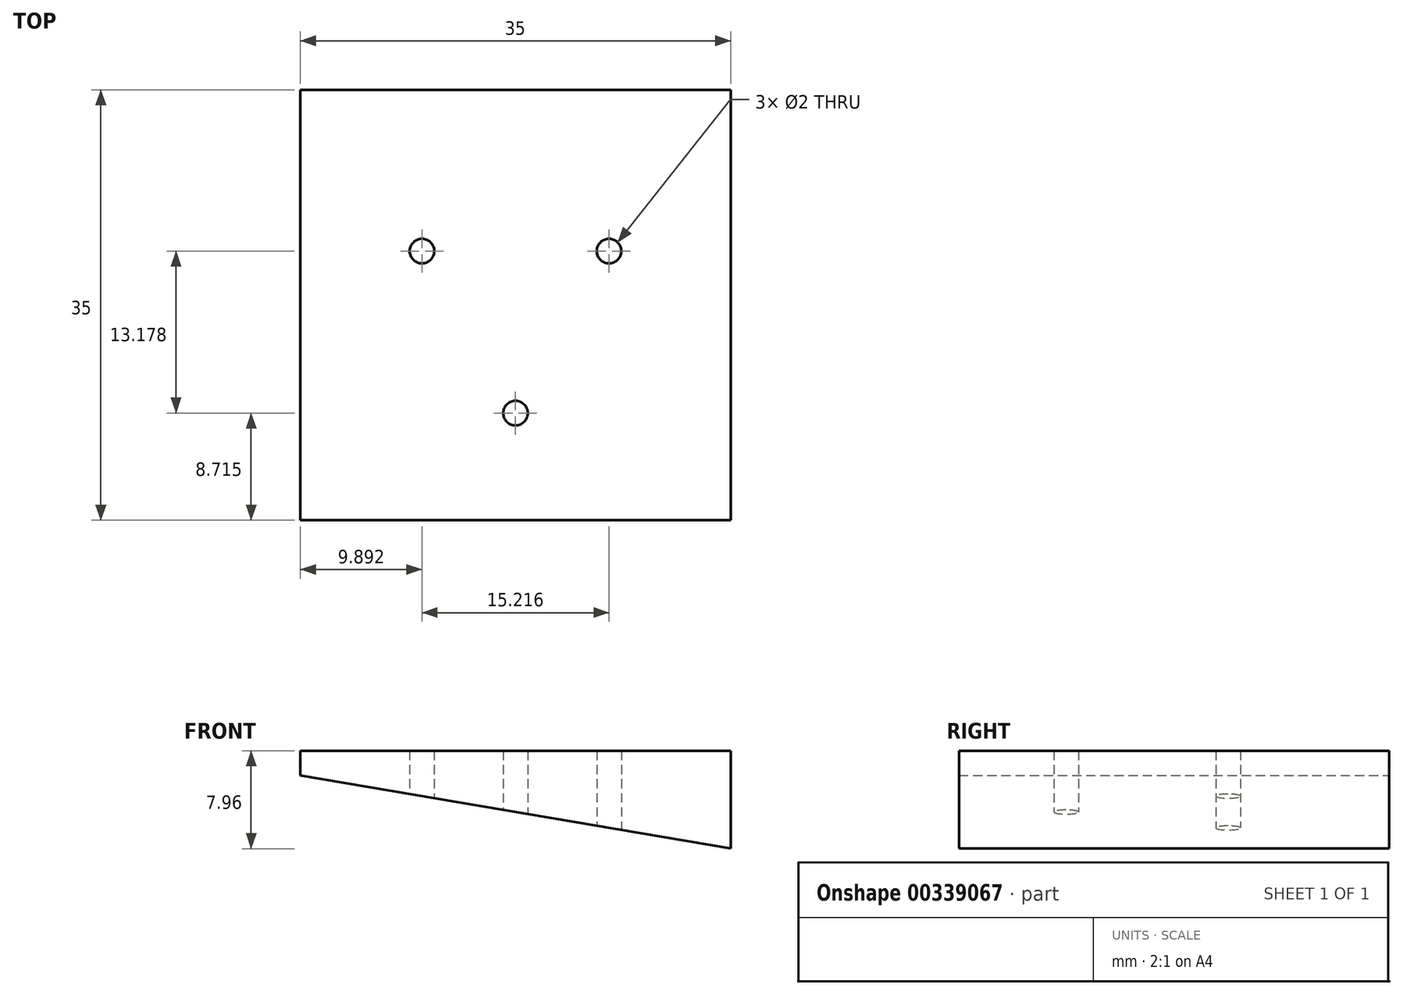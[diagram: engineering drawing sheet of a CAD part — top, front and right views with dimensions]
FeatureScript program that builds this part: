
annotation { "Feature Type Name" : "Feature", "Feature Type Description" : "" }
export const myFeature = defineFeature(function(context is Context, id is Id, definition is map)
    precondition{}
    {
        {
            var Q0;
            Q0=qCreatedBy(makeId("Top.planeOp"),FACE);
            var sketch = newSketch(context, id + "F0", { "sketchPlane" : qUnion([Q0])});
            skLineSegment(sketch, "E0.bottom", {"start": v(17.5, -17.5) * mm, "end": v(-17.5, -17.5) * mm});
            skLineSegment(sketch, "E0.top", {"start": v(17.5, 17.5) * mm, "end": v(-17.5, 17.5) * mm});
            skLineSegment(sketch, "E0.left", {"start": v(17.5, -17.5) * mm, "end": v(17.5, 17.5) * mm});
            skLineSegment(sketch, "E0.right", {"start": v(-17.5, -17.5) * mm, "end": v(-17.5, 17.5) * mm});
            skPoint(sketch, "E0.middle", {"position": v(0, 0) * mm});
            skCircle(sketch, "E1", {"center": v(0, 0) * mm, "radius": 11.29 * mm});
            skCircle(sketch, "E2", {"center": v(0, -8.79) * mm, "radius": 1 * mm});
            skCircle(sketch, "E3.1.0", {"center": v(7.6, 4.4) * mm, "radius": 1 * mm});
            skCircle(sketch, "E3.2.0", {"center": v(-7.6, 4.4) * mm, "radius": 1 * mm});
            skSolve(sketch);
        }
        {
            var Q0;
            Q0=makeQuery(id+"F0.imprint","IMPRINT",FACE,{"disambiguationData":[TD([[makeQuery(id+"F0.imprint","IMPRINT",EDGE,{"derivedFrom":sQuery(id+"F0.wireOp",EDGE,"E0.bottom")}),-1.0]])]});
            var Q1;
            Q1=makeQuery(id+"F0.imprint","IMPRINT",FACE,{"disambiguationData":[TD([[makeQuery(id+"F0.imprint","IMPRINT",EDGE,{"derivedFrom":sQuery(id+"F0.wireOp",EDGE,"E1")}),1.0]])]});
            extrude(context, id + "F1", {"entities" : qUnion([Q0, Q1]), "depth" : 2 * mm, "offsetDistance" : 25 * mm});
        }
        {
            var Q0;
            Q0=makeQuery(id+"F1.opExtrude","SWEPT_FACE",FACE,{"disambiguationData":[OSD([sQuery(id+"F0.wireOp",EDGE,"E0.bottom")])]});
            var sketch = newSketch(context, id + "F2", { "sketchPlane" : qUnion([Q0])});
            skLineSegment(sketch, "E4", {"start": v(17.5, 0) * mm, "end": v(17.5, -5.96) * mm});
            skLineSegment(sketch, "E5", {"start": v(17.5, -5.96) * mm, "end": v(-17.5, 0) * mm});
            skSolve(sketch);
        }
        {
            var Q0;
            Q0=makeQuery(id+"F2.imprint","IMPRINT",FACE,{"disambiguationData":[TD([[makeQuery(id+"F2.imprint","IMPRINT",EDGE,{"derivedFrom":sQuery(id+"F2.wireOp",EDGE,"E4")}),-1.0]])]});
            var Q1;
            Q1=makeQuery(id+"F1.opExtrude","SWEPT_FACE",FACE,{"disambiguationData":[OSD([sQuery(id+"F0.wireOp",EDGE,"E0.top")])]});
            extrude(context, id + "F3", {"entities" : qUnion([Q0]), "operationType" : NewBodyOperationType.ADD, "endBound" : BoundingType.UP_TO_SURFACE, "oppositeDirection" : true, "depth" : 33.1 * mm, "endBoundEntityFace" : qUnion([Q1]), "offsetDistance" : 25 * mm});
        }
        {
            var Q0;
            Q0=makeQuery(id+"F3.boolean.opBoolean","SPLIT",FACE,{"disambiguationData":[TD([makeQuery(id+"F1.opExtrude","SWEPT_FACE",FACE,{"disambiguationData":[OSD([sQuery(id+"F0.wireOp",EDGE,"E3.1.0")])]})])],"derivedFrom":makeQuery(id+"F3.opExtrude","SWEPT_FACE",FACE,{"disambiguationData":[OSD([sQuery(id+"F0.wireOp",EDGE,"E0.bottom")])]})});
            var Q1;
            Q1=makeQuery(id+"F3.boolean.opBoolean","SPLIT",FACE,{"disambiguationData":[TD([makeQuery(id+"F1.opExtrude","SWEPT_FACE",FACE,{"disambiguationData":[OSD([sQuery(id+"F0.wireOp",EDGE,"E2")])]})])],"derivedFrom":makeQuery(id+"F3.opExtrude","SWEPT_FACE",FACE,{"disambiguationData":[OSD([sQuery(id+"F0.wireOp",EDGE,"E0.bottom")])]})});
            var Q2;
            Q2=makeQuery(id+"F3.boolean.opBoolean","SPLIT",FACE,{"disambiguationData":[TD([makeQuery(id+"F1.opExtrude","SWEPT_FACE",FACE,{"disambiguationData":[OSD([sQuery(id+"F0.wireOp",EDGE,"E3.2.0")])]})])],"derivedFrom":makeQuery(id+"F3.opExtrude","SWEPT_FACE",FACE,{"disambiguationData":[OSD([sQuery(id+"F0.wireOp",EDGE,"E0.bottom")])]})});
            extrude(context, id + "F4", {"entities" : qUnion([Q0, Q1, Q2]), "operationType" : NewBodyOperationType.REMOVE, "oppositeDirection" : true, "depth" : 25 * mm, "offsetDistance" : 25 * mm});
        }
    });
